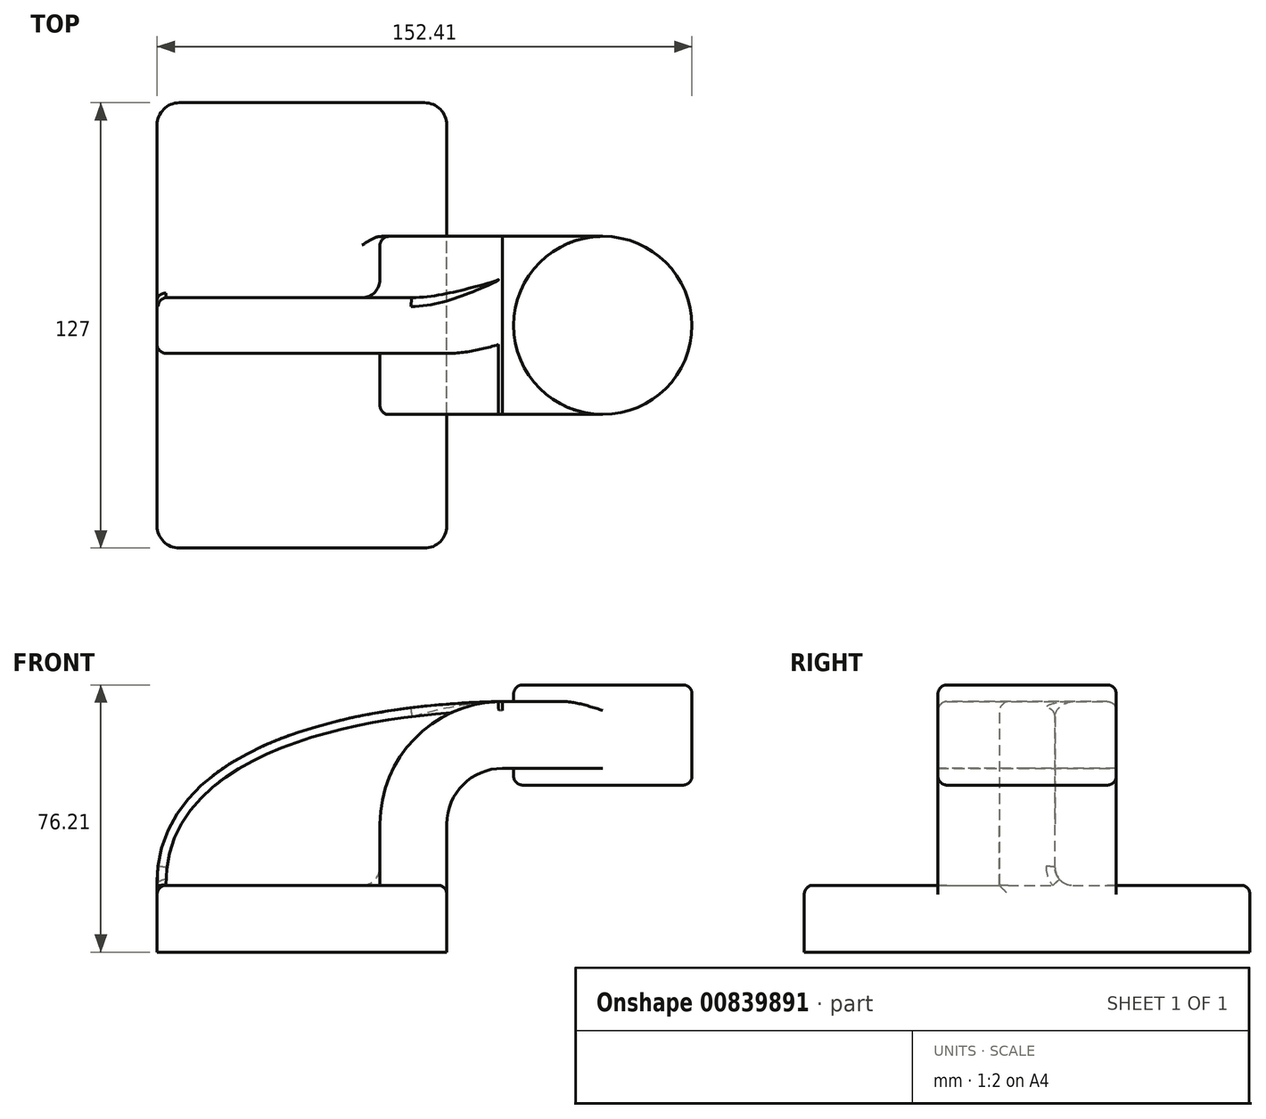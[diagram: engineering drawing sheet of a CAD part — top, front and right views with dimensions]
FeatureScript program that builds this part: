
annotation { "Feature Type Name" : "Feature", "Feature Type Description" : "" }
export const myFeature = defineFeature(function(context is Context, id is Id, definition is map)
    precondition{}
    {
        {
            var Q0;
            Q0=qCreatedBy(makeId("Front.planeOp"),FACE);
            var sketch = newSketch(context, id + "F0", { "sketchPlane" : qUnion([Q0])});
            skLineSegment(sketch, "E0.bottom", {"start": v(-41.28, -9.53) * mm, "end": v(41.28, -9.53) * mm});
            skLineSegment(sketch, "E0.top", {"start": v(-41.28, 9.53) * mm, "end": v(41.28, 9.53) * mm});
            skLineSegment(sketch, "E0.left", {"start": v(-41.28, -9.53) * mm, "end": v(-41.28, 9.53) * mm});
            skLineSegment(sketch, "E0.right", {"start": v(41.28, -9.53) * mm, "end": v(41.28, 9.53) * mm});
            skPoint(sketch, "E0.middle", {"position": v(0, 0) * mm});
            skLineSegment(sketch, "E1.bottom", {"start": v(60.33, 38.1) * mm, "end": v(111.13, 38.1) * mm});
            skLineSegment(sketch, "E1.top", {"start": v(60.33, 66.68) * mm, "end": v(111.12, 66.68) * mm});
            skLineSegment(sketch, "E1.left", {"start": v(60.33, 38.1) * mm, "end": v(60.32, 66.68) * mm});
            skLineSegment(sketch, "E1.right", {"start": v(111.12, 38.1) * mm, "end": v(111.12, 66.68) * mm});
            skPoint(sketch, "E1.middle", {"position": v(85.72, 52.39) * mm});
            skLineSegment(sketch, "E2", {"start": v(41.28, 9.53) * mm, "end": v(41.28, 27) * mm});
            skArc(sketch, "E3", {"start": v(41.27, 27) * mm, "mid": v(45.92, 38.23) * mm, "end": v(57.15, 42.88) * mm});
            skLineSegment(sketch, "E4", {"start": v(57.15, 42.88) * mm, "end": v(85.72, 42.88) * mm});
            skLineSegment(sketch, "E5.0", {"start": v(57.15, 61.93) * mm, "end": v(85.72, 61.93) * mm});
            skArc(sketch, "E5.1", {"start": v(22.22, 27) * mm, "mid": v(32.45, 51.7) * mm, "end": v(57.15, 61.93) * mm});
            skLineSegment(sketch, "E5.2", {"start": v(22.22, 9.53) * mm, "end": v(22.22, 27) * mm});
            skLineSegment(sketch, "E6", {"start": v(85.73, 38.1) * mm, "end": v(85.72, 66.68) * mm});
            skFitSpline(sketch, "E7", {"points": [v(-41.28, 9.53) * mm, v(57.15, 61.93) * mm], "startDerivative": vector(-1.97, 118.43) * mm, "endDerivative": vector(130.76, 1.88) * mm});
            skSolve(sketch);
        }
        {
            var Q0;
            Q0=makeQuery(id+"F0.imprint","IMPRINT",FACE,{"disambiguationData":[TD([[makeQuery(id+"F0.imprint","IMPRINT",EDGE,{"derivedFrom":sQuery(id+"F0.wireOp",EDGE,"E0.bottom")}),1.0]])]});
            extrude(context, id + "F1", {"entities" : qUnion([Q0]), "endBound" : BoundingType.SYMMETRIC, "depth" : 127 * mm, "offsetDistance" : 25.4 * mm});
        }
        {
            var Q0;
            {var subQ1=sQuery(id+"F0.wireOp",EDGE,"E2");Q0=makeQuery(id+"F0.imprint","IMPRINT",FACE,{"disambiguationData":[TD([[makeQuery(id+"F0.imprint","IMPRINT",EDGE,{"derivedFrom":subQ1}),1.0]])]});}
            var Q1;
            {var subQ0=sQuery(id+"F0.wireOp",EDGE,"E4");var subQ1=sQuery(id+"F0.wireOp",EDGE,"E1.left");var subQ2=makeQuery(id+"F0.imprint","INTERSECT",VERTEX,{"derivedFrom":[subQ1,subQ0]});Q1=makeQuery(id+"F0.imprint","IMPRINT",FACE,{"disambiguationData":[TD([[makeQuery(id+"F0.imprint","IMPRINT",EDGE,{"disambiguationData":[TD([[subQ2,-1.0]])],"derivedFrom":subQ1}),-1.0]])]});}
            extrude(context, id + "F2", {"entities" : qUnion([Q0, Q1]), "operationType" : NewBodyOperationType.ADD, "endBound" : BoundingType.SYMMETRIC, "depth" : 50.8 * mm, "offsetDistance" : 25.4 * mm});
        }
        {
            var Q0;
            {var subQ3=sQuery(id+"F0.wireOp",EDGE,"E5.2");Q0=makeQuery(id+"F0.imprint","IMPRINT",FACE,{"disambiguationData":[TD([[makeQuery(id+"F0.imprint","IMPRINT",EDGE,{"derivedFrom":subQ3}),1.0]])]});}
            extrude(context, id + "F3", {"entities" : qUnion([Q0]), "operationType" : NewBodyOperationType.ADD, "endBound" : BoundingType.SYMMETRIC, "depth" : 15.88 * mm, "offsetDistance" : 25.4 * mm});
        }
        {
            var Q0;
            {var subQ4=sQuery(id+"F0.wireOp",EDGE,"E1.right");Q0=makeQuery(id+"F0.imprint","IMPRINT",FACE,{"disambiguationData":[TD([[makeQuery(id+"F0.imprint","IMPRINT",EDGE,{"derivedFrom":subQ4}),1.0]])]});}
            var Q1;
            Q1=sQuery(id+"F0.wireOp",EDGE,"E6");
            revolve(context, id + "F4", {"operationType" : NewBodyOperationType.ADD, "surfaceOperationType" : NewSurfaceOperationType.NEW, "entities" : qUnion([Q0]), "axis" : qUnion([Q1]), "revolveType" : RevolveType.FULL});
        }
        {
            var Q0;
            Q0=makeQuery(id+"F1.opExtrude","CAP_EDGE",EDGE,{"disambiguationData":[OSD([sQuery(id+"F0.wireOp",EDGE,"E0.right")])],"isStart":false});
            var Q1;
            Q1=makeQuery(id+"F1.opExtrude","CAP_EDGE",EDGE,{"disambiguationData":[OSD([sQuery(id+"F0.wireOp",EDGE,"E0.left")])],"isStart":false});
            var Q2;
            Q2=makeQuery(id+"F1.opExtrude","CAP_EDGE",EDGE,{"disambiguationData":[OSD([sQuery(id+"F0.wireOp",EDGE,"E0.right")])],"isStart":true});
            var Q3;
            Q3=makeQuery(id+"F1.opExtrude","CAP_EDGE",EDGE,{"disambiguationData":[OSD([sQuery(id+"F0.wireOp",EDGE,"E0.left")])],"isStart":true});
            fillet(context, id + "F5", {"entities" : qUnion([Q0, Q1, Q2, Q3]), "radius" : 6.35 * mm, "tangentPropagation" : true, "allowEdgeOverflow" : false});
        }
        {
            var Q0;
            Q0=makeQuery(id+"F3.opExtrude","CAP_EDGE",EDGE,{"disambiguationData":[OSD([sQuery(id+"F0.wireOp",EDGE,"E0.top")])],"isStart":false});
            var Q1;
            Q1=makeQuery(id+"F2.opExtrude","CAP_EDGE",EDGE,{"disambiguationData":[OSD([sQuery(id+"F0.wireOp",EDGE,"E0.top")])],"isStart":false});
            var Q2;
            {var subQ0=sQuery(id+"F0.wireOp",EDGE,"E0.top");var subQ1=sQuery(id+"F0.wireOp",EDGE,"E7");var subQ2=sQuery(id+"F0.wireOp",EDGE,"E5.2");var subQ3=sQuery(id+"F0.wireOp",EDGE,"E5.1");Q2=makeQuery(id+"F3.boolean.opBoolean","SPLIT",EDGE,{"disambiguationData":[TD([makeQuery(id+"F3.opExtrude","CAP_FACE",FACE,{"disambiguationData":[OSD([subQ0,subQ3,subQ2,subQ1])],"isStart":false})])],"derivedFrom":makeQuery(id+"F2.opExtrude","SWEPT_EDGE",EDGE,{"disambiguationData":[OSD([subQ0,subQ2])]})});}
            var Q3;
            Q3=makeQuery(id+"F2.opExtrude","CAP_EDGE",EDGE,{"disambiguationData":[OSD([sQuery(id+"F0.wireOp",EDGE,"E0.top")])],"isStart":true});
            var Q4;
            {var subQ0=sQuery(id+"F0.wireOp",EDGE,"E0.top");var subQ1=sQuery(id+"F0.wireOp",EDGE,"E7");var subQ2=sQuery(id+"F0.wireOp",EDGE,"E5.2");var subQ3=sQuery(id+"F0.wireOp",EDGE,"E5.1");Q4=makeQuery(id+"F3.boolean.opBoolean","SPLIT",EDGE,{"disambiguationData":[TD([makeQuery(id+"F3.opExtrude","CAP_FACE",FACE,{"disambiguationData":[OSD([subQ0,subQ3,subQ2,subQ1])],"isStart":true})])],"derivedFrom":makeQuery(id+"F2.opExtrude","SWEPT_EDGE",EDGE,{"disambiguationData":[OSD([subQ0,subQ2])]})});}
            var Q5;
            Q5=makeQuery(id+"F3.opExtrude","CAP_EDGE",EDGE,{"disambiguationData":[OSD([sQuery(id+"F0.wireOp",EDGE,"E0.top")])],"isStart":true});
            fillet(context, id + "F6", {"entities" : qUnion([Q0, Q1, Q2, Q3, Q4, Q5]), "radius" : 5.08 * mm, "tangentPropagation" : true, "allowEdgeOverflow" : false});
        }
        {
            var Q0;
            Q0=makeQuery(id+"F3.opExtrude","CAP_EDGE",EDGE,{"disambiguationData":[OSD([sQuery(id+"F0.wireOp",EDGE,"E5.1")])],"isStart":false});
            var Q1;
            Q1=makeQuery(id+"F3.opExtrude","CAP_EDGE",EDGE,{"disambiguationData":[OSD([sQuery(id+"F0.wireOp",EDGE,"E5.2")])],"isStart":false});
            var Q2;
            Q2=makeQuery(id+"F3.opExtrude","CAP_EDGE",EDGE,{"disambiguationData":[OSD([sQuery(id+"F0.wireOp",EDGE,"E5.1")])],"isStart":true});
            var Q3;
            Q3=makeQuery(id+"F3.opExtrude","CAP_EDGE",EDGE,{"disambiguationData":[OSD([sQuery(id+"F0.wireOp",EDGE,"E5.2")])],"isStart":true});
            fillet(context, id + "F7", {"entities" : qUnion([Q0, Q1, Q2, Q3]), "radius" : 5.08 * mm, "tangentPropagation" : true, "allowEdgeOverflow" : false});
        }
        {
            var Q0;
            Q0=makeQuery(id+"F4.opRevolve","SWEPT_EDGE",EDGE,{"disambiguationData":[OSD([sQuery(id+"F0.wireOp",EDGE,"E1.top"),sQuery(id+"F0.wireOp",EDGE,"E1.right")])]});
            var Q1;
            Q1=makeQuery(id+"F4.opRevolve","SWEPT_EDGE",EDGE,{"disambiguationData":[OSD([sQuery(id+"F0.wireOp",EDGE,"E1.bottom"),sQuery(id+"F0.wireOp",EDGE,"E1.right")])]});
            fillet(context, id + "F8", {"entities" : qUnion([Q0, Q1]), "radius" : 2.54 * mm, "tangentPropagation" : true, "allowEdgeOverflow" : false});
        }
        {
            var Q0;
            {var subQ0=sQuery(id+"F0.wireOp",EDGE,"E0.right");var subQ1=sQuery(id+"F0.wireOp",EDGE,"E2");var subQ2=sQuery(id+"F0.wireOp",EDGE,"E0.top");Q0=makeQuery(id+"F2.boolean.opBoolean","SPLIT",EDGE,{"disambiguationData":[TD([makeQuery(id+"F1.opExtrude","CAP_FACE",FACE,{"disambiguationData":[OSD([sQuery(id+"F0.wireOp",EDGE,"E0.bottom"),subQ2,sQuery(id+"F0.wireOp",EDGE,"E0.left"),subQ0])],"isStart":false})])],"derivedFrom":makeQuery(id+"F1.opExtrude","SWEPT_EDGE",EDGE,{"disambiguationData":[OSD([subQ2,subQ0,subQ1])]})});}
            var Q1;
            Q1=makeQuery(id+"F3.opExtrude","CAP_EDGE",EDGE,{"disambiguationData":[OSD([sQuery(id+"F0.wireOp",EDGE,"E7")])],"isStart":false});
            var Q2;
            {var subQ0=sQuery(id+"F0.wireOp",EDGE,"E7");Q2=makeQuery(id+"F7.opFillet","BLEND_EDGE",EDGE,{"blendedFrom":[makeQuery(id+"F3.opExtrude","CAP_EDGE",EDGE,{"disambiguationData":[OSD([sQuery(id+"F0.wireOp",EDGE,"E5.1")])],"isStart":false}),makeQuery(id+"F3.boolean.opBoolean","MERGE",FACE,{"derivedFrom":[makeQuery(id+"F2.opExtrude","SWEPT_FACE",FACE,{"disambiguationData":[OSD([subQ0])]}),makeQuery(id+"F3.opExtrude","SWEPT_FACE",FACE,{"disambiguationData":[OSD([subQ0])]})]})],"blendedInto":[makeQuery(id+"F3.boolean.opBoolean","MERGE",FACE,{"derivedFrom":[makeQuery(id+"F2.opExtrude","SWEPT_FACE",FACE,{"disambiguationData":[OSD([subQ0])]}),makeQuery(id+"F3.opExtrude","SWEPT_FACE",FACE,{"disambiguationData":[OSD([subQ0])]})]})]});}
            var Q3;
            {var subQ0=sQuery(id+"F0.wireOp",EDGE,"E7");Q3=makeQuery(id+"F7.opFillet","BLEND_EDGE",EDGE,{"blendedFrom":[makeQuery(id+"F3.opExtrude","CAP_EDGE",EDGE,{"disambiguationData":[OSD([sQuery(id+"F0.wireOp",EDGE,"E5.1")])],"isStart":true}),makeQuery(id+"F3.boolean.opBoolean","MERGE",FACE,{"derivedFrom":[makeQuery(id+"F2.opExtrude","SWEPT_FACE",FACE,{"disambiguationData":[OSD([subQ0])]}),makeQuery(id+"F3.opExtrude","SWEPT_FACE",FACE,{"disambiguationData":[OSD([subQ0])]})]})],"blendedInto":[makeQuery(id+"F3.boolean.opBoolean","MERGE",FACE,{"derivedFrom":[makeQuery(id+"F2.opExtrude","SWEPT_FACE",FACE,{"disambiguationData":[OSD([subQ0])]}),makeQuery(id+"F3.opExtrude","SWEPT_FACE",FACE,{"disambiguationData":[OSD([subQ0])]})]})]});}
            var Q4;
            Q4=makeQuery(id+"F3.opExtrude","CAP_EDGE",EDGE,{"disambiguationData":[OSD([sQuery(id+"F0.wireOp",EDGE,"E7")])],"isStart":true});
            var Q5;
            {var subQ0=sQuery(id+"F0.wireOp",EDGE,"E0.left");var subQ1=sQuery(id+"F0.wireOp",EDGE,"E0.top");var subQ2=sQuery(id+"F0.wireOp",EDGE,"E7");Q5=makeQuery(id+"F3.boolean.opBoolean","SPLIT",EDGE,{"disambiguationData":[TD([makeQuery(id+"F1.opExtrude","CAP_FACE",FACE,{"disambiguationData":[OSD([sQuery(id+"F0.wireOp",EDGE,"E0.bottom"),subQ1,subQ0,sQuery(id+"F0.wireOp",EDGE,"E0.right")])],"isStart":true})])],"derivedFrom":makeQuery(id+"F1.opExtrude","SWEPT_EDGE",EDGE,{"disambiguationData":[OSD([subQ1,subQ0,subQ2])]})});}
            var Q6;
            Q6=makeQuery(id+"F2.opExtrude","CAP_EDGE",EDGE,{"disambiguationData":[OSD([sQuery(id+"F0.wireOp",EDGE,"E5.0")])],"isStart":true});
            var Q7;
            Q7=makeQuery(id+"F2.opExtrude","CAP_EDGE",EDGE,{"disambiguationData":[OSD([sQuery(id+"F0.wireOp",EDGE,"E5.1")])],"isStart":true});
            var Q8;
            Q8=makeQuery(id+"F2.opExtrude","CAP_EDGE",EDGE,{"disambiguationData":[OSD([sQuery(id+"F0.wireOp",EDGE,"E7")])],"isStart":true});
            var Q9;
            Q9=makeQuery(id+"F2.opExtrude","CAP_EDGE",EDGE,{"disambiguationData":[OSD([sQuery(id+"F0.wireOp",EDGE,"E5.0")])],"isStart":false});
            var Q10;
            Q10=makeQuery(id+"F2.opExtrude","CAP_EDGE",EDGE,{"disambiguationData":[OSD([sQuery(id+"F0.wireOp",EDGE,"E7")])],"isStart":false});
            var Q11;
            Q11=makeQuery(id+"F2.opExtrude","CAP_EDGE",EDGE,{"disambiguationData":[OSD([sQuery(id+"F0.wireOp",EDGE,"E5.1")])],"isStart":false});
            fillet(context, id + "F9", {"entities" : qUnion([Q0, Q1, Q2, Q3, Q4, Q5, Q6, Q7, Q8, Q9, Q10, Q11]), "radius" : 2.54 * mm, "tangentPropagation" : true, "allowEdgeOverflow" : false});
        }
    });
